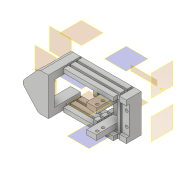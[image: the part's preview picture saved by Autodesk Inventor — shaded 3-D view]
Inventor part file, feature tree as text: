
AUTODESK INVENTOR PART (.ipt)
format: ipt  version: 2019.4 (Build 234330000, 330)  size: 541,184 bytes
history: native  units: mm
features: plane x15, sketch x15, extrude x14, projected_geometry x12, other x2, mirror x1, fillet x1
ambient origin geometry x8: Origin, YZ Plane, XZ Plane, XY Plane, X Axis, Y Axis, Z Axis, Center Point
bodies: Solid1 (feature_tree)
feature tree (60):
  plane  "Work Plane1"
  plane  "Work Plane2"
  plane  "Work Plane4"
  extrude  "Extrusion4"  Depth=4.0mm TaperAngle=0.0deg
  plane  "Work Plane5"
  extrude  "Extrusion5"  Depth=5.0mm TaperAngle=0.0deg
  plane  "Work Plane11"
  extrude  "Extrusion8"  Depth=5.0mm
  plane  "Work Plane7"
  extrude  "Extrusion9"  Depth=2.0mm
  plane  "Work Plane3"
  plane  "Work Plane13"
  extrude  "Extrusion10"  Depth=0.6mm
  plane  "Work Plane12"
  extrude  "Extrusion11"  Depth=4.0mm
  extrude  "Extrusion14"  Depth=1.0mm
  extrude  "Extrusion15"  Depth=2.9mm
  mirror  "Mirror2"
  extrude  "Extrusion17"  TaperAngle=0.0deg  [1 undecoded]
  extrude  "Extrusion18"  TaperAngle=0.0deg  [1 undecoded]
  sketch  "Sketch20"  dims[d101=7.0mm d102=0.0mm]
  extrude  "Extrusion19"  TaperAngle=0.0deg  [1 undecoded]
  extrude  "Extrusion20"  Depth=19.0mm
  fillet  "Fillet1"  Radius=22.0mm
  extrude  "Extrusion21"  Depth=4.0mm
  extrude  "Extrusion22"  TaperAngle=0.0deg  [1 undecoded]
  sketch  "Sketch5"  dims[d28=15.0mm d29=0.0mm d37=4.0mm d38=0.0mm]
  sketch  "Sketch6"  dims[d43=7.0mm d60=5.0mm d61=0.0mm]
  sketch  "Sketch9"  dims[d62=4.0mm d63=5.0mm]
  sketch  "Sketch10"  dims[d64=9.0mm d65=0.0mm d66=2.0mm]
  sketch  "Sketch11"  dims[d67=0.6mm d68=0.6mm]
  projected_geometry  "Projected Loop9"
  sketch  "Sketch12"  dims[d70=15.0mm d71=0.0mm d72=4.0mm]
  projected_geometry  "Projected Loop10"
  sketch  "Sketch15"  dims[d73=0.0mm d77=1.0mm]
  projected_geometry  "Projected Loop13"
  projected_geometry  "Projected Loop14"
  projected_geometry  "Projected Loop15"
  sketch  "Sketch16"  dims[d78=2.9mm d79=2.9mm]
  projected_geometry  "Projected Loop16"
  plane  "Work Plane14"
  plane  "Work Plane15"
  plane  "Work Plane16"
  plane  "Work Plane17"
  plane  "Work Plane18"
  plane  "Work Plane19"
  sketch  "Sketch18"  dims[d80=4.0mm d81=0.0mm d92=0.0mm]
  sketch  "Sketch19"  dims[d93=5.0mm d94=0.0mm]
  sketch  "Sketch21"  dims[d104=10.0mm d105=0.0mm d106=19.0mm d107=22.0mm]
  projected_geometry  "Projected Loop17"
  projected_geometry  "Projected Loop18"
  projected_geometry  "Projected Loop19"
  sketch  "Sketch22"  dims[d108=28.0mm d109=4.0mm]
  projected_geometry  "Projected Loop20"
  sketch  "Sketch23"  dims[d110=4.0mm d111=0.0mm]
  projected_geometry  "Projected Loop21"
  sketch  "Sketch24"  dims[d112=2.0mm d113=0.6mm d115=5.0mm d117=2.9mm d118=7.0mm d119=10.0mm d120=0.0mm d121=4.0mm d122=5.0mm d123=0.6mm d124=2.0mm d125=2.0mm d130=10.0mm d131=0.0mm d132=1.0mm d133=0.0mm d134=30.0mm d135=8.0mm d136=0.0mm d137=0.0mm d138=10.0mm d139=0.0mm d140=5.0mm d141=30.0mm d143=7.0mm d144=10.0mm d146=10.0mm d148=17.0mm d149=0.0mm d150=16.0mm d151=0.0mm d152=0.0mm d153=5.0mm d154=10.0mm d155=0.0mm d156=5.0mm d157=0.0mm]
  projected_geometry  "Projected Loop22"
  other  "Assembly_Opentrons_Autofocus_v2.iam"
  other  "00_MGN12C, LINEAR GUIDE BLOCK:1"
note: 4 required parameter values undecoded (feature->parameter linkage not recoverable at this tier; creation-order binding heuristic only, values carry confidence <= 0.55)
